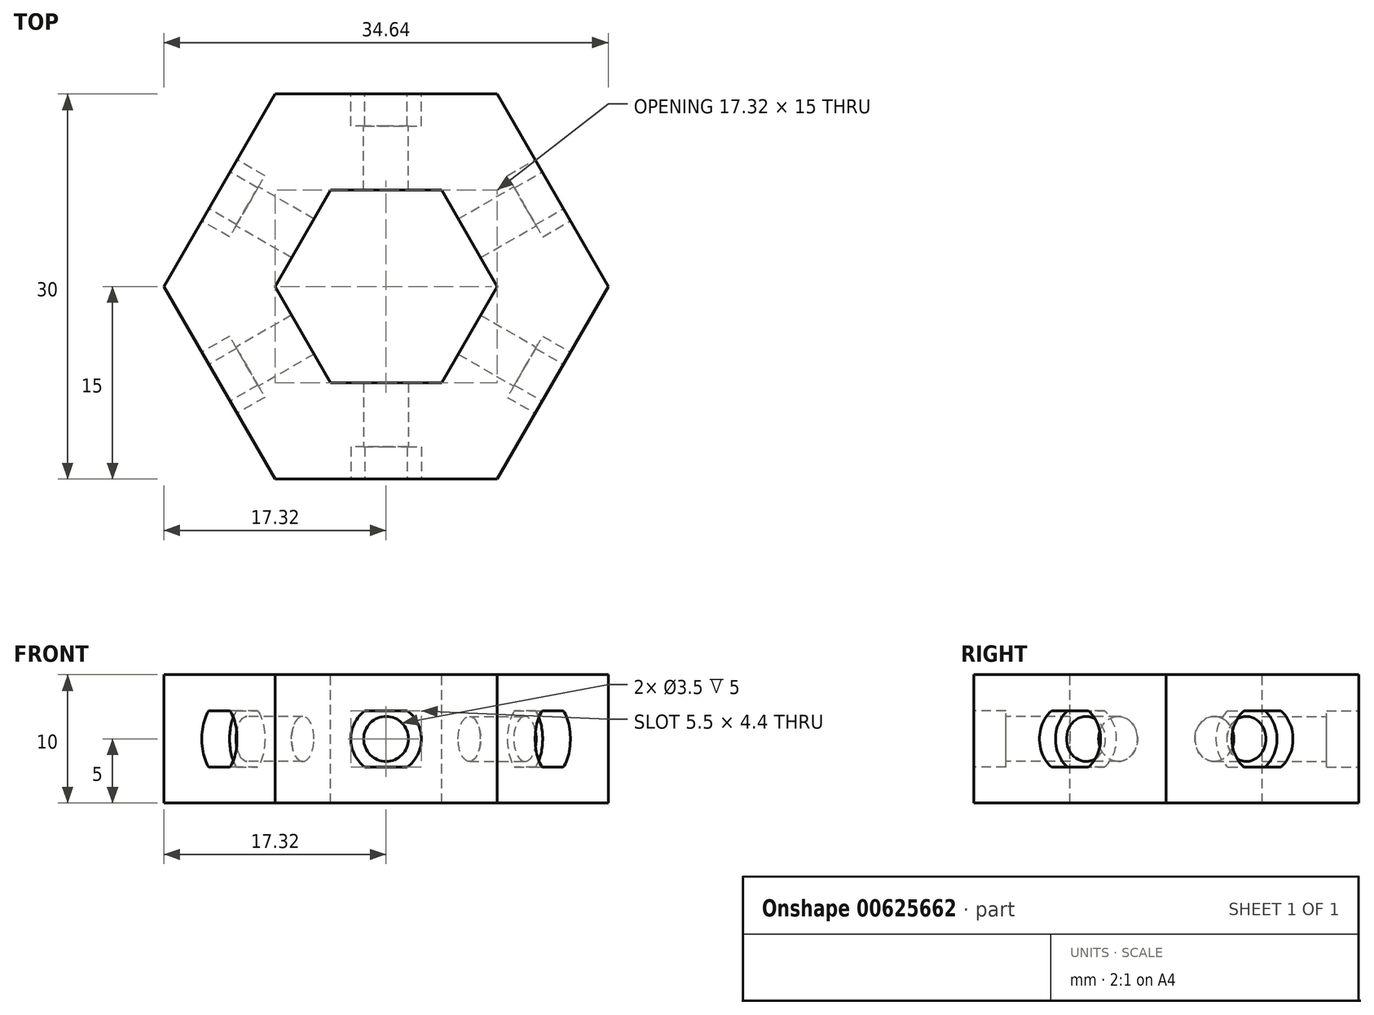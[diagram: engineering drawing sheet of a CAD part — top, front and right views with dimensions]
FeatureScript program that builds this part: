
annotation { "Feature Type Name" : "Feature", "Feature Type Description" : "" }
export const myFeature = defineFeature(function(context is Context, id is Id, definition is map)
    precondition{}
    {
        {
            var Q0;
            Q0=qCreatedBy(makeId("Top.planeOp"),FACE);
            var sketch = newSketch(context, id + "F0", { "sketchPlane" : qUnion([Q0])});
            skCircle(sketch, "E0.cCircle", {"center": v(0, 0) * mm, "radius": 15 * mm, "construction": true});
            skLineSegment(sketch, "E0.0", {"start": v(8.66, -15) * mm, "end": v(-8.66, -15) * mm});
            skLineSegment(sketch, "E0.1", {"start": v(-8.66, -15) * mm, "end": v(-17.32, 0) * mm});
            skLineSegment(sketch, "E0.2", {"start": v(-17.32, 0) * mm, "end": v(-8.66, 15) * mm});
            skLineSegment(sketch, "E0.3", {"start": v(-8.66, 15) * mm, "end": v(8.66, 15) * mm});
            skLineSegment(sketch, "E0.4", {"start": v(8.66, 15) * mm, "end": v(17.32, 0) * mm});
            skLineSegment(sketch, "E0.5", {"start": v(17.32, 0) * mm, "end": v(8.66, -15) * mm});
            skPoint(sketch, "E0.0.midPoint", {"position": v(0, -15) * mm});
            skLineSegment(sketch, "E1", {"start": v(0, 0) * mm, "end": v(-8.66, -15) * mm});
            skLineSegment(sketch, "E2", {"start": v(0, 0) * mm, "end": v(8.66, -15) * mm});
            skSolve(sketch);
        }
        {
            var Q0;
            Q0=makeQuery(id+"F0.imprint","IMPRINT",FACE,{"disambiguationData":[TD([[makeQuery(id+"F0.imprint","IMPRINT",EDGE,{"derivedFrom":sQuery(id+"F0.wireOp",EDGE,"E0.0")}),-1.0]])]});
            extrude(context, id + "F1", {"entities" : qUnion([Q0]), "depth" : 10 * mm, "offsetDistance" : 25 * mm});
        }
        {
            var Q0;
            Q0=makeQuery(id+"F1.opExtrude","SWEPT_FACE",FACE,{"disambiguationData":[OSD([sQuery(id+"F0.wireOp",EDGE,"E0.0")])]});
            var sketch = newSketch(context, id + "F2", { "sketchPlane" : qUnion([Q0])});
            skPoint(sketch, "E3", {"position": v(-8.66, 5) * mm});
            skPoint(sketch, "E4", {"position": v(0, 10) * mm});
            skPoint(sketch, "E5", {"position": v(0, 5) * mm});
            skCircle(sketch, "E6", {"center": v(0, 5) * mm, "radius": 2.75 * mm});
            skPoint(sketch, "E7", {"position": v(0, 7.2) * mm});
            skPoint(sketch, "E8", {"position": v(0, 2.8) * mm});
            skLineSegment(sketch, "E9", {"start": v(1.65, 7.2) * mm, "end": v(-1.65, 7.2) * mm});
            skLineSegment(sketch, "E10", {"start": v(1.65, 2.8) * mm, "end": v(-1.65, 2.8) * mm});
            skCircle(sketch, "E11", {"center": v(0, 5) * mm, "radius": 1.75 * mm});
            skSolve(sketch);
        }
        {
            var Q0;
            Q0=makeQuery(id+"F2.imprint","IMPRINT",FACE,{"disambiguationData":[TD([[makeQuery(id+"F2.imprint","IMPRINT",EDGE,{"derivedFrom":sQuery(id+"F2.wireOp",EDGE,"E11")}),1.0]])]});
            extrude(context, id + "F3", {"entities" : qUnion([Q0]), "operationType" : NewBodyOperationType.REMOVE, "oppositeDirection" : true, "depth" : 25 * mm, "offsetDistance" : 25 * mm});
        }
        {
            var Q0;
            {var subQ1=sQuery(id+"F2.wireOp",EDGE,"E9");Q0=makeQuery(id+"F2.imprint","IMPRINT",FACE,{"disambiguationData":[TD([[makeQuery(id+"F2.imprint","IMPRINT",EDGE,{"derivedFrom":subQ1}),1.0]])]});}
            extrude(context, id + "F4", {"entities" : qUnion([Q0]), "operationType" : NewBodyOperationType.REMOVE, "oppositeDirection" : true, "depth" : 2.5 * mm, "offsetDistance" : 25 * mm});
        }
        {
            var Q0;
            Q0=qCreatedBy(makeId("Front.planeOp"),FACE);
            var sketch = newSketch(context, id + "F5", { "sketchPlane" : qUnion([Q0])});
            skLineSegment(sketch, "E12", {"start": v(0, 0) * mm, "end": v(0, 15.5) * mm, "construction": true});
            skSolve(sketch);
        }
        {
            var Q0;
            Q0=makeQuery(id+"F1.opExtrude","SWEPT_BODY",BODY,{"disambiguationData":[OSD([sQuery(id+"F0.wireOp",EDGE,"E0.0"),sQuery(id+"F0.wireOp",EDGE,"E1"),sQuery(id+"F0.wireOp",EDGE,"E2")])]});
            var Q1;
            Q1=sQuery(id+"F5.wireOp",EDGE,"E12");
            circularPattern(context, id + "F6", {"operationType" : NewBodyOperationType.ADD, "entities" : qUnion([Q0]), "axis" : qUnion([Q1]), "angle" : 360 * degree, "instanceCount" : 6, "equalSpace" : true});
        }
        {
            var Q0;
            {var subQ0=makeQuery(id+"F1.opExtrude","CAP_FACE",FACE,{"disambiguationData":[OSD([sQuery(id+"F0.wireOp",EDGE,"E0.0"),sQuery(id+"F0.wireOp",EDGE,"E1"),sQuery(id+"F0.wireOp",EDGE,"E2")])],"isStart":false});Q0=makeQuery(id+"F6.boolean.opBoolean","MERGE",FACE,{"derivedFrom":[subQ0,makeQuery(id+"F6.opPattern","COPY",FACE,{"derivedFrom":subQ0,"instanceName":"1"}),makeQuery(id+"F6.opPattern","COPY",FACE,{"derivedFrom":subQ0,"instanceName":"2"}),makeQuery(id+"F6.opPattern","COPY",FACE,{"derivedFrom":subQ0,"instanceName":"3"}),makeQuery(id+"F6.opPattern","COPY",FACE,{"derivedFrom":subQ0,"instanceName":"4"}),makeQuery(id+"F6.opPattern","COPY",FACE,{"derivedFrom":subQ0,"instanceName":"5"})]});}
            var sketch = newSketch(context, id + "F7", { "sketchPlane" : qUnion([Q0])});
            skCircle(sketch, "E13.cCircle", {"center": v(0, 0) * mm, "radius": 7.5 * mm, "construction": true});
            skLineSegment(sketch, "E13.0", {"start": v(4.33, -7.5) * mm, "end": v(-4.33, -7.5) * mm});
            skLineSegment(sketch, "E13.1", {"start": v(-4.33, -7.5) * mm, "end": v(-8.66, 0) * mm});
            skLineSegment(sketch, "E13.2", {"start": v(-8.66, 0) * mm, "end": v(-4.33, 7.5) * mm});
            skLineSegment(sketch, "E13.3", {"start": v(-4.33, 7.5) * mm, "end": v(4.33, 7.5) * mm});
            skLineSegment(sketch, "E13.4", {"start": v(4.33, 7.5) * mm, "end": v(8.66, 0) * mm});
            skLineSegment(sketch, "E13.5", {"start": v(8.66, 0) * mm, "end": v(4.33, -7.5) * mm});
            skPoint(sketch, "E13.0.midPoint", {"position": v(0, -7.5) * mm});
            skSolve(sketch);
        }
        {
            var Q0;
            Q0=makeQuery(id+"F7.imprint","IMPRINT",FACE,{"disambiguationData":[TD([[makeQuery(id+"F7.imprint","IMPRINT",EDGE,{"derivedFrom":sQuery(id+"F7.wireOp",EDGE,"E13.0")}),-1.0]])]});
            extrude(context, id + "F8", {"entities" : qUnion([Q0]), "operationType" : NewBodyOperationType.REMOVE, "oppositeDirection" : true, "depth" : 25 * mm, "offsetDistance" : 25 * mm});
        }
    });
